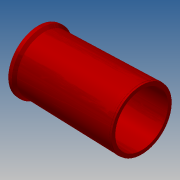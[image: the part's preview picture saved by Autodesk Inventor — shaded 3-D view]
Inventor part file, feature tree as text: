
AUTODESK INVENTOR PART (.ipt)
format: ipt  version: 2017.3 (Build 213257000, 257)  size: 249,344 bytes
history: native  units: in
note: dims shown in document units (in); Inventor stores cm internally (conversion verified against a paired STEP export)
features: revolve x1, fillet x1, sketch x1
ambient origin geometry x8: Origin, YZ Plane, XZ Plane, XY Plane, X Axis, Y Axis, Z Axis, Center Point
bodies: Solid1 (feature_tree)
feature tree (3):
  revolve  "Revolution1"  [1 undecoded]
  fillet  "Fillet1"  Radius=28.5in
  sketch  "Sketch1"  dims[d0=55.8661in d1=26.0in d2=28.5in d3=32.48in d4=2.0in d5=1.0in d6=1.0in d7=32.48in d8=30.0in d9=1.0in d10=4.0in d11=12.0in d12=12.0in d13=48.0in d14=2.0779in d15=90.0deg d16=0.0312in d17=1.0in d18=45.0deg d19=32.75in d23=1.0in d24=45.0deg d25=32.75in]
note: 1 required parameter value undecoded (feature->parameter linkage not recoverable at this tier; creation-order binding heuristic only, values carry confidence <= 0.55)
